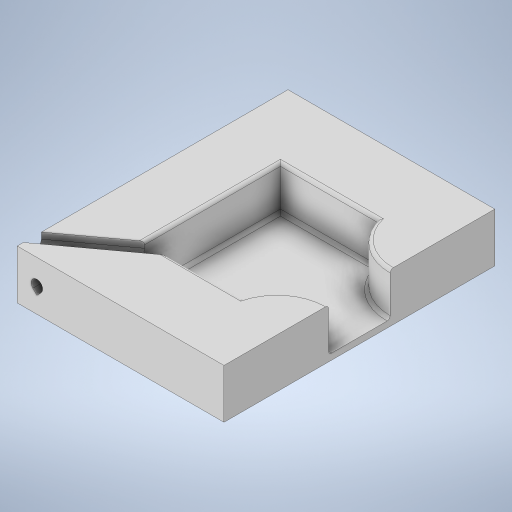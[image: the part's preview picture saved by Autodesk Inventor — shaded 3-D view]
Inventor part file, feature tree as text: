
AUTODESK INVENTOR PART (.ipt)
format: ipt  version: 2024 (Build 280153000, 153)  size: 738,816 bytes
history: native  units: in
note: dims shown in document units (in); Inventor stores cm internally (conversion verified against a paired STEP export)
features: sketch x9, projected_geometry x9, extrude x8, fillet x4, mirror x2, plane x1, emboss x1
ambient origin geometry x8: Origin, YZ Plane, XZ Plane, XY Plane, X Axis, Y Axis, Z Axis, Center Point
bodies: Solid1 (feature_tree)
feature tree (34):
  extrude  "Extrusion1"  Depth=5.5in
  extrude  "Extrusion2"  Depth=2.374in
  extrude  "Extrusion3"  Depth=0.1in
  extrude  "Extrusion4"  Depth=1.25in
  plane  "Work Plane1"
  extrude  "Extrusion5"  Depth=0.2in
  mirror  "Mirror1"
  emboss  "Emboss1"
  fillet  "Fillet1"  Radius=0.2in
  extrude  "Extrusion6"  Depth=1.0in
  fillet  "Fillet2"  Radius=1.0in
  extrude  "Extrusion7"  Depth=0.2362in
  mirror  "Mirror2"
  extrude  "Extrusion8"  Depth=0.2362in
  fillet  "Fillet4"  Radius=0.4in
  fillet  "Fillet5"  Radius=0.4331in
  sketch  "Sketch1"  dims[d0=4.2in d1=5.5in]
  sketch  "Sketch2"  dims[d2=1.0in d3=0.0in d4=2.374in]
  projected_geometry  "Projected Loop1"
  sketch  "Sketch3"  dims[d5=1.5827in d7=0.1in]
  projected_geometry  "Projected Loop2"
  projected_geometry  "Projected Loop3"
  sketch  "Sketch4"  dims[d8=0.875in d9=0.0in d10=1.25in]
  sketch  "Sketch5"  dims[d12=0.875in d13=0.0in d14=0.2in d15=0.2in]
  projected_geometry  "Projected Loop4"
  sketch  "Sketch6"  dims[d16=0.45in d17=1.0in d18=1.0in]
  projected_geometry  "Projected Loop5"
  sketch  "Sketch8"  dims[d19=0.45in d20=0.2362in]
  projected_geometry  "Projected Loop7"
  projected_geometry  "Projected Loop8"
  sketch  "Sketch9"  dims[d21=0.4331in d22=0.0in d23=0.2362in d24=0.4in d25=0.4331in d26=0.0in]
  projected_geometry  "Projected Loop9"
  sketch  "Sketch10"  dims[d27=0.85in d28=3.125in d29=0.0157in d30=0.0in d31=0.0625in d32=0.5in d33=0.125in d34=0.25in d35=0.0in d36=0.125in d37=0.25in d38=0.0in d40=4.5in d41=0.25in d42=1.0in d43=0.0in d45=0.25in d48=0.125in]
  projected_geometry  "Projected Loop10"
